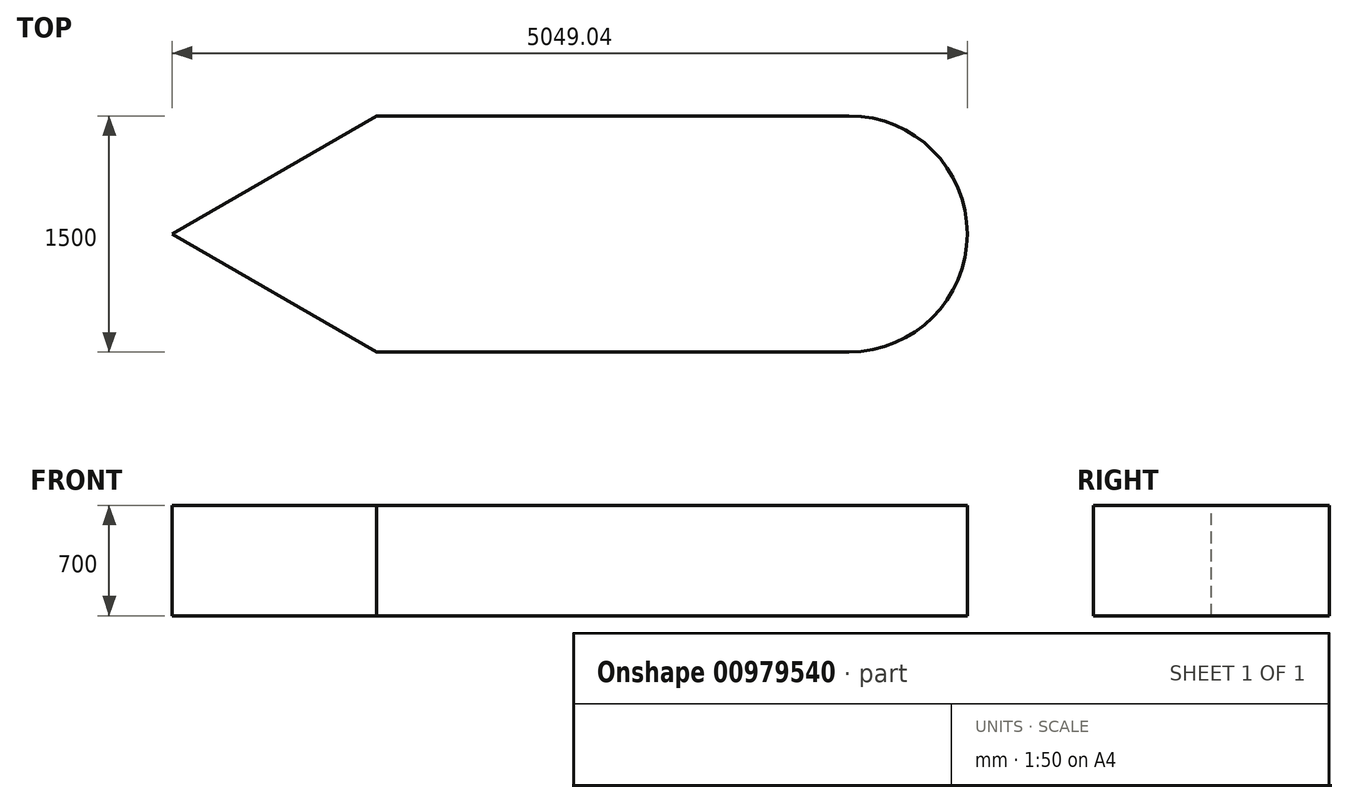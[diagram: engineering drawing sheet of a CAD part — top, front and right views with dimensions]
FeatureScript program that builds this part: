
annotation { "Feature Type Name" : "Feature", "Feature Type Description" : "" }
export const myFeature = defineFeature(function(context is Context, id is Id, definition is map)
    precondition{}
    {
        {
            var Q0;
            Q0=qCreatedBy(makeId("Top.planeOp"),FACE);
            var sketch = newSketch(context, id + "F0", { "sketchPlane" : qUnion([Q0])});
            skLineSegment(sketch, "E0", {"start": v(0, 0) * mm, "end": v(-3000, 0) * mm});
            skLineSegment(sketch, "E1", {"start": v(-3000, 0) * mm, "end": v(-4299.04, -750) * mm});
            skLineSegment(sketch, "E2", {"start": v(-4299.04, -750) * mm, "end": v(-3000, -1500) * mm});
            skLineSegment(sketch, "E3", {"start": v(-3000, -1500) * mm, "end": v(0, -1500) * mm});
            skArc(sketch, "E4", {"start": v(0, -1500) * mm, "mid": v(750, -750) * mm, "end": v(0, 0) * mm});
            skLineSegment(sketch, "E5", {"start": v(1476.82, -750) * mm, "end": v(-5706.18, -750) * mm, "construction": true});
            skPoint(sketch, "E5.startSnap0", {"position": v(750, -750) * mm});
            skSolve(sketch);
        }
        {
            var Q0;
            Q0=makeQuery(id+"F0.imprint","IMPRINT",FACE,{"disambiguationData":[TD([[makeQuery(id+"F0.imprint","IMPRINT",EDGE,{"derivedFrom":sQuery(id+"F0.wireOp",EDGE,"E0")}),1.0]])]});
            extrude(context, id + "F1", {"entities" : qUnion([Q0]), "oppositeDirection" : true, "depth" : 1200 * mm, "offsetDistance" : 25 * mm});
        }
        {
            var Q0;
            Q0=makeQuery(id+"F1.opExtrude","CAP_FACE",FACE,{"disambiguationData":[OSD([sQuery(id+"F0.wireOp",EDGE,"E0"),sQuery(id+"F0.wireOp",EDGE,"E1"),sQuery(id+"F0.wireOp",EDGE,"E2"),sQuery(id+"F0.wireOp",EDGE,"E3"),sQuery(id+"F0.wireOp",EDGE,"E4")])],"isStart":false});
            extrude(context, id + "F2", {"entities" : qUnion([Q0]), "operationType" : NewBodyOperationType.REMOVE, "oppositeDirection" : true, "depth" : 500 * mm, "offsetDistance" : 25 * mm});
        }
        {
            var Q0;
            Q0=makeQuery(id+"F2.boolean.opBoolean","COPY",VERTEX,{"derivedFrom":makeQuery(id+"F2.opExtrude","CAP_VERTEX",VERTEX,{"disambiguationData":[OSD([sQuery(id+"F0.wireOp",EDGE,"E0"),sQuery(id+"F0.wireOp",EDGE,"E1")])],"isStart":false})});
            var Q1;
            Q1=makeQuery(id+"F2.boolean.opBoolean","COPY",VERTEX,{"derivedFrom":makeQuery(id+"F2.opExtrude","CAP_VERTEX",VERTEX,{"disambiguationData":[OSD([sQuery(id+"F0.wireOp",EDGE,"E2"),sQuery(id+"F0.wireOp",EDGE,"E3")])],"isStart":false})});
            var Q2;
            Q2=makeQuery(id+"F1.opExtrude","CAP_VERTEX",VERTEX,{"disambiguationData":[OSD([sQuery(id+"F0.wireOp",EDGE,"E2"),sQuery(id+"F0.wireOp",EDGE,"E3")])],"isStart":true});
            cPlane(context, id + "F3", {"entities" : qUnion([Q0, Q1, Q2]), "cplaneType" : CPlaneType.THREE_POINT, "offset" : 25 * mm, "width" : 150 * mm, "height" : 150 * mm});
        }
    });
